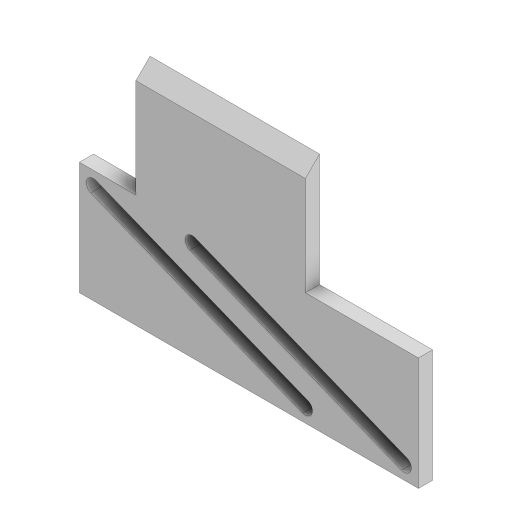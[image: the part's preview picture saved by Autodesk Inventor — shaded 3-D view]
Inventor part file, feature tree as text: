
AUTODESK INVENTOR PART (.ipt)
format: ipt  version: 2024.2 (Build 282272000, 272)  size: 128,000 bytes
history: native  units: in
note: dims shown in document units (in); Inventor stores cm internally (conversion verified against a paired STEP export)
features: extrude x1, chamfer x1, sketch x1
ambient origin geometry x8: Origin, YZ Plane, XZ Plane, XY Plane, X Axis, Y Axis, Z Axis, Center Point
bodies: Solid1 (feature_tree)
feature tree (3):
  extrude  "Extrusion1"  Depth=2.0in
  chamfer  "Chamfer1"  Distance=6.0in
  sketch  "Sketch2"  dims[d0=3.0in d1=2.0in d2=6.0in d3=2.0in d4=1.0in d5=0.25in d6=0.25in d7=0.25in d8=0.25in d9=0.25in d10=0.25in d11=0.25in d12=0.25in d13=0.25in d14=0.0in d15=0.25in d16=0.125in d17=45.0deg]
